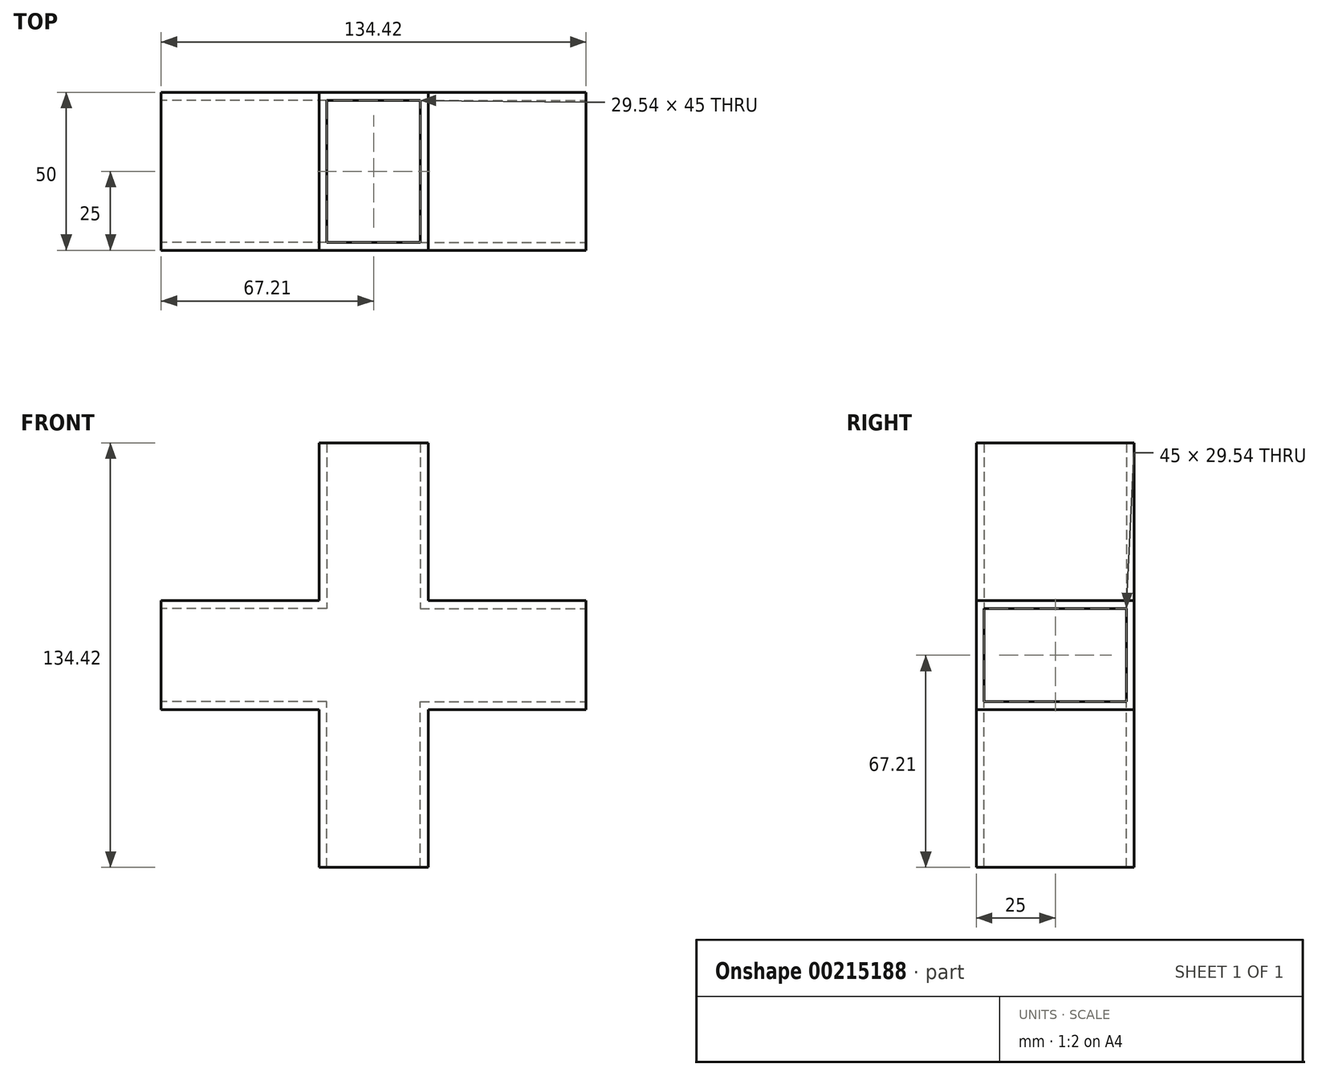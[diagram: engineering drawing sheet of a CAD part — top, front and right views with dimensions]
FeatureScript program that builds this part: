
annotation { "Feature Type Name" : "Feature", "Feature Type Description" : "" }
export const myFeature = defineFeature(function(context is Context, id is Id, definition is map)
    precondition{}
    {
        {
            var Q0;
            Q0=qCreatedBy(makeId("Front.planeOp"),FACE);
            var sketch = newSketch(context, id + "F0", { "sketchPlane" : qUnion([Q0])});
            skLineSegment(sketch, "E0", {"start": v(0, 67.21) * mm, "end": v(-17.27, 67.21) * mm});
            skLineSegment(sketch, "E1", {"start": v(-17.27, 67.21) * mm, "end": v(-17.27, 17.27) * mm});
            skLineSegment(sketch, "E2", {"start": v(-17.27, 17.27) * mm, "end": v(-67.21, 17.27) * mm});
            skLineSegment(sketch, "E3", {"start": v(-67.21, 17.27) * mm, "end": v(-67.21, 0) * mm});
            skLineSegment(sketch, "E4", {"start": v(17.64, 0) * mm, "end": v(0, 0) * mm, "construction": true});
            skLineSegment(sketch, "E5", {"start": v(0, 0) * mm, "end": v(0, -21.17) * mm, "construction": true});
            skLineSegment(sketch, "E6.MirrorCS", {"start": v(0, 67.21) * mm, "end": v(17.27, 67.21) * mm});
            skLineSegment(sketch, "E7.MirrorCS", {"start": v(17.27, 17.27) * mm, "end": v(67.21, 17.27) * mm});
            skLineSegment(sketch, "E8.MirrorCS", {"start": v(67.21, 17.27) * mm, "end": v(67.21, 0) * mm});
            skLineSegment(sketch, "E9.MirrorCS", {"start": v(17.27, 67.21) * mm, "end": v(17.27, 17.27) * mm});
            skLineSegment(sketch, "E10.MirrorCS", {"start": v(17.27, -67.21) * mm, "end": v(17.27, -17.27) * mm});
            skLineSegment(sketch, "E11.MirrorCS", {"start": v(67.21, -17.27) * mm, "end": v(67.21, 0) * mm});
            skLineSegment(sketch, "E12.MirrorCS", {"start": v(17.27, -17.27) * mm, "end": v(67.21, -17.27) * mm});
            skLineSegment(sketch, "E13.MirrorCS", {"start": v(-67.21, -17.27) * mm, "end": v(-67.21, 0) * mm});
            skLineSegment(sketch, "E14.MirrorCS", {"start": v(-17.27, -17.27) * mm, "end": v(-67.21, -17.27) * mm});
            skLineSegment(sketch, "E15.MirrorCS", {"start": v(0, -67.21) * mm, "end": v(17.27, -67.21) * mm});
            skLineSegment(sketch, "E16.MirrorCS", {"start": v(0, -67.21) * mm, "end": v(-17.27, -67.21) * mm});
            skLineSegment(sketch, "E17.MirrorCS", {"start": v(-17.27, -67.21) * mm, "end": v(-17.27, -17.27) * mm});
            skSolve(sketch);
        }
        {
            var Q0;
            Q0 = qSketchRegion(id + "F0", true);
            extrude(context, id + "F1", {"entities" : qUnion([Q0]), "depth" : 50 * mm, "offsetDistance" : 25 * mm});
        }
        {
            var Q0;
            Q0=makeQuery(id+"F1.opExtrude","SWEPT_FACE",FACE,{"disambiguationData":[OSD([sQuery(id+"F0.wireOp",EDGE,"E8.MirrorCS"),sQuery(id+"F0.wireOp",EDGE,"E11.MirrorCS")])]});
            var Q1;
            Q1=makeQuery(id+"F1.opExtrude","SWEPT_FACE",FACE,{"disambiguationData":[OSD([sQuery(id+"F0.wireOp",EDGE,"E0"),sQuery(id+"F0.wireOp",EDGE,"E6.MirrorCS")])]});
            var Q2;
            Q2=makeQuery(id+"F1.opExtrude","SWEPT_FACE",FACE,{"disambiguationData":[OSD([sQuery(id+"F0.wireOp",EDGE,"E3"),sQuery(id+"F0.wireOp",EDGE,"E13.MirrorCS")])]});
            var Q3;
            Q3=makeQuery(id+"F1.opExtrude","SWEPT_FACE",FACE,{"disambiguationData":[OSD([sQuery(id+"F0.wireOp",EDGE,"E15.MirrorCS"),sQuery(id+"F0.wireOp",EDGE,"E16.MirrorCS")])]});
            shell(context, id + "F2", {"entities" : qUnion([Q0, Q1, Q2, Q3]), "thickness" : 2.5 * mm});
        }
    });
